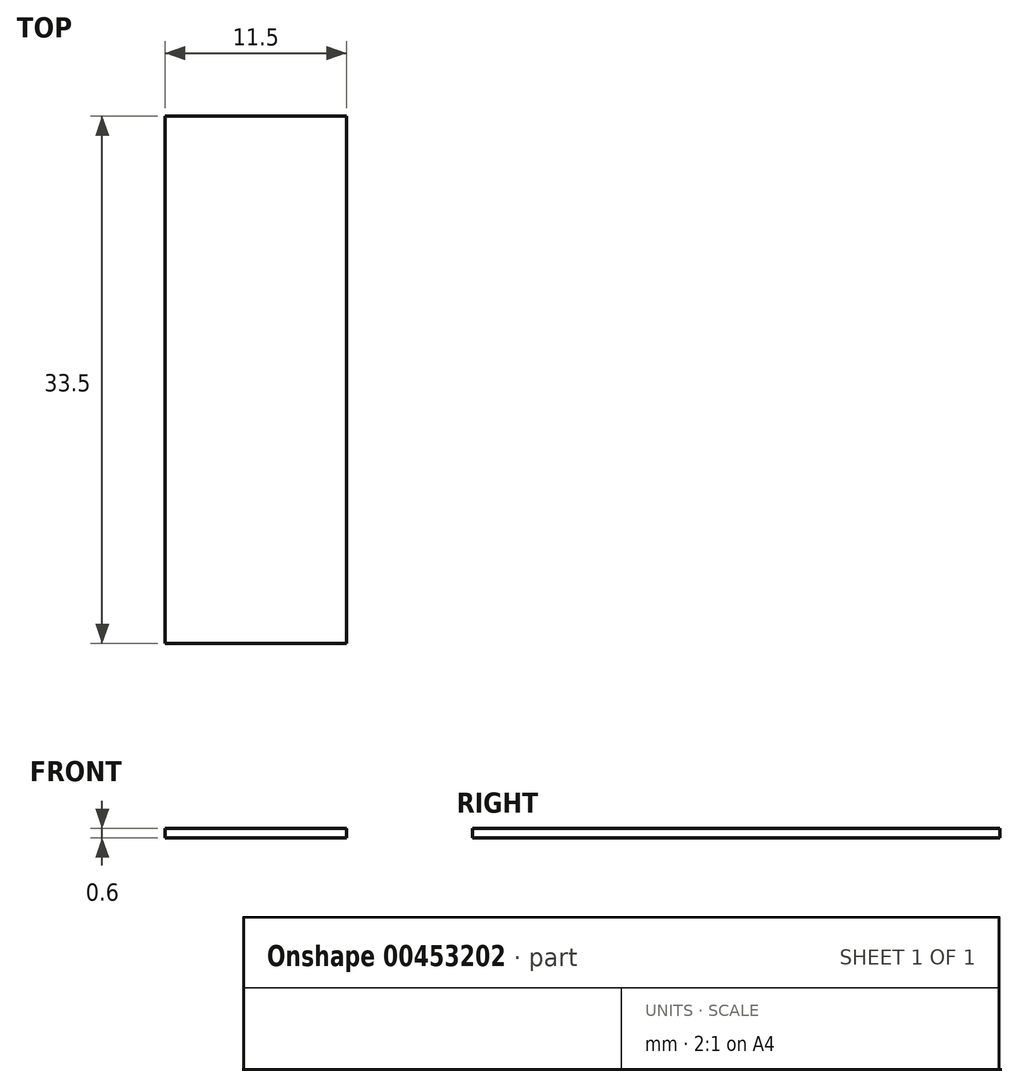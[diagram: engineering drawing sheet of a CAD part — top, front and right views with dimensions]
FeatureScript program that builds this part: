
annotation { "Feature Type Name" : "Feature", "Feature Type Description" : "" }
export const myFeature = defineFeature(function(context is Context, id is Id, definition is map)
    precondition{}
    {
        {
            var Q0;
            Q0=qCreatedBy(makeId("Top.planeOp"),FACE);
            var sketch = newSketch(context, id + "F0", { "sketchPlane" : qUnion([Q0])});
            skLineSegment(sketch, "E0.bottom", {"start": v(-15.9, -7.06) * mm, "end": v(-4.4, -7.06) * mm});
            skLineSegment(sketch, "E0.top", {"start": v(-15.9, -40.56) * mm, "end": v(-4.4, -40.56) * mm});
            skLineSegment(sketch, "E0.left", {"start": v(-15.9, -7.06) * mm, "end": v(-15.9, -40.56) * mm});
            skLineSegment(sketch, "E0.right", {"start": v(-4.4, -7.06) * mm, "end": v(-4.4, -40.56) * mm});
            skSolve(sketch);
        }
        {
            var Q0;
            Q0=makeQuery(id+"F0.imprint","IMPRINT",FACE,{"disambiguationData":[TD([[makeQuery(id+"F0.imprint","IMPRINT",EDGE,{"derivedFrom":sQuery(id+"F0.wireOp",EDGE,"E0.bottom")}),-1.0]])]});
            extrude(context, id + "F1", {"entities" : qUnion([Q0]), "depth" : 0.6 * mm});
        }
    });
